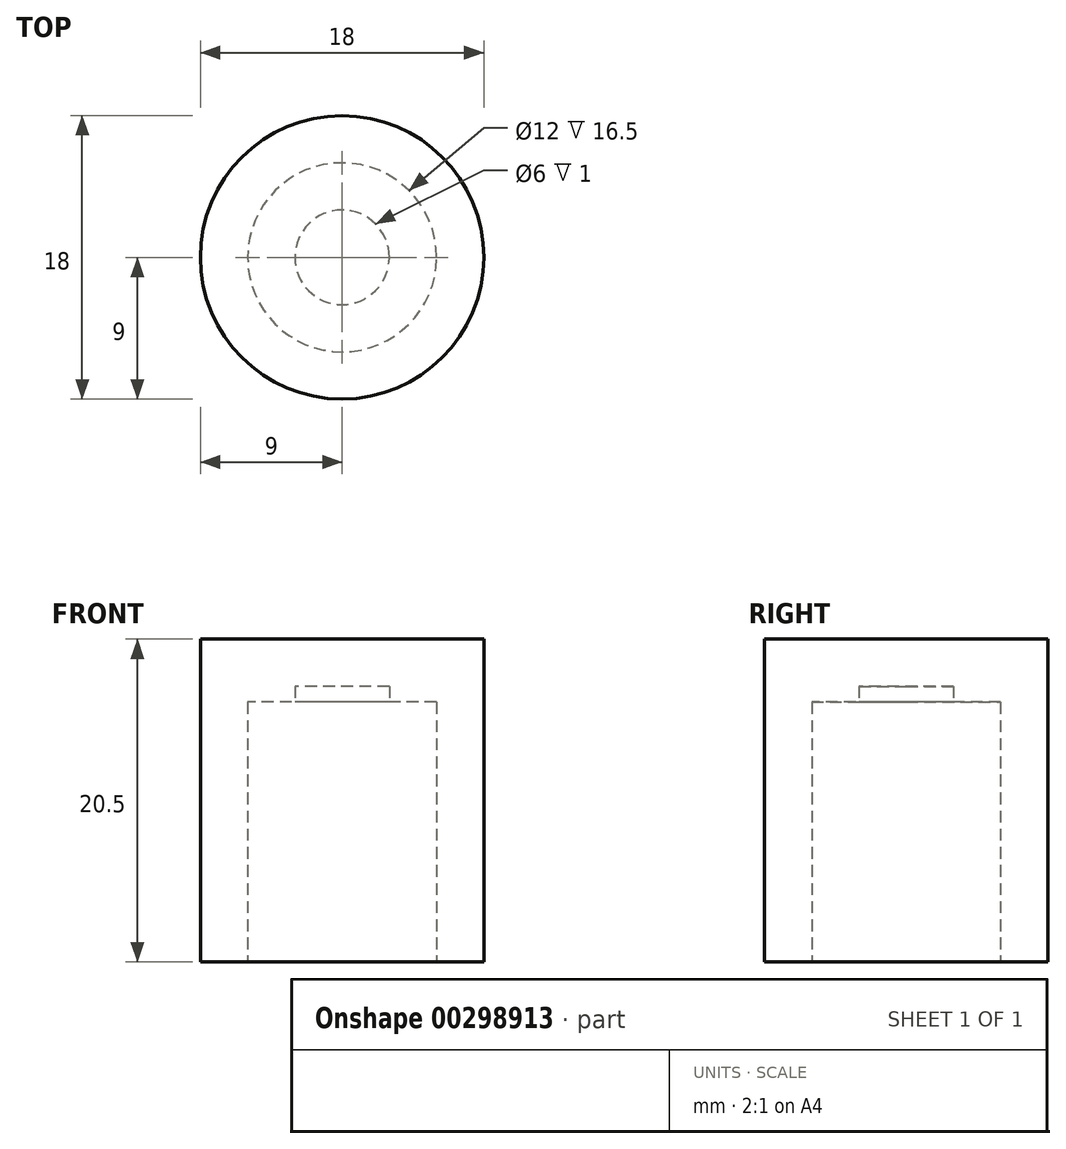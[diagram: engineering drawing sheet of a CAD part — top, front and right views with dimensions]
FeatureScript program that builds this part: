
annotation { "Feature Type Name" : "Feature", "Feature Type Description" : "" }
export const myFeature = defineFeature(function(context is Context, id is Id, definition is map)
    precondition{}
    {
        {
            var Q0;
            Q0=qCreatedBy(makeId("Top.planeOp"),FACE);
            var sketch = newSketch(context, id + "F0", { "sketchPlane" : qUnion([Q0])});
            skCircle(sketch, "E0", {"center": v(0, 0) * mm, "radius": 9 * mm});
            skSolve(sketch);
        }
        {
            var Q0;
            Q0 = qSketchRegion(id + "F0", true);
            extrude(context, id + "F1", {"entities" : qUnion([Q0]), "offsetDistance" : 25 * mm, "depth" : 20.5 * mm});
        }
        {
            var Q0;
            Q0=qCreatedBy(makeId("Top.planeOp"),FACE);
            var sketch = newSketch(context, id + "F2", { "sketchPlane" : qUnion([Q0])});
            skCircle(sketch, "E1", {"center": v(0, 0) * mm, "radius": 6 * mm});
            skSolve(sketch);
        }
        {
            var Q0;
            Q0 = qSketchRegion(id + "F2", true);
            extrude(context, id + "F3", {"entities" : qUnion([Q0]), "operationType" : NewBodyOperationType.REMOVE, "offsetDistance" : 25 * mm, "depth" : 16.5 * mm});
        }
        {
            var Q0;
            Q0=qCreatedBy(makeId("Top.planeOp"),FACE);
            var sketch = newSketch(context, id + "F4", { "sketchPlane" : qUnion([Q0])});
            skCircle(sketch, "E2", {"center": v(0, 0) * mm, "radius": 3 * mm});
            skSolve(sketch);
        }
        {
            var Q0;
            Q0 = qSketchRegion(id + "F4", true);
            extrude(context, id + "F5", {"entities" : qUnion([Q0]), "operationType" : NewBodyOperationType.REMOVE, "offsetDistance" : 25 * mm, "depth" : 17.5 * mm});
        }
    });
